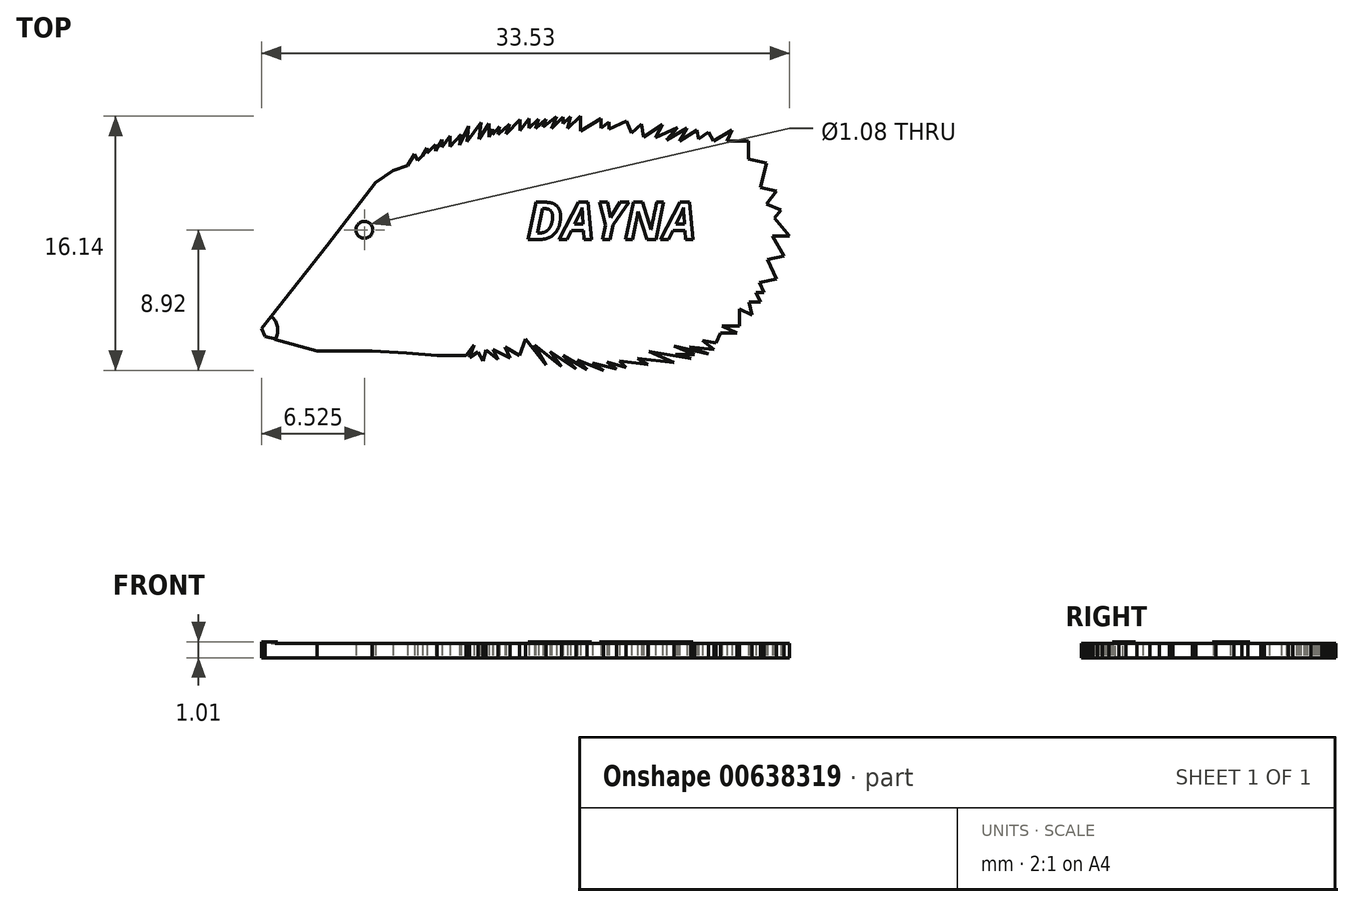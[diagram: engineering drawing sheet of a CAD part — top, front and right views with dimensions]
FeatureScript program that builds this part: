
annotation { "Feature Type Name" : "Feature", "Feature Type Description" : "" }
export const myFeature = defineFeature(function(context is Context, id is Id, definition is map)
    precondition{}
    {
        {
            var Q0;
            Q0=qCreatedBy(makeId("Top.planeOp"),FACE);
            var sketch = newSketch(context, id + "F0", { "sketchPlane" : qUnion([Q0])});
            skLineSegment(sketch, "E0", {"start": v(-31.15, -0.16) * mm, "end": v(-27, 5.13) * mm});
            skLineSegment(sketch, "E1", {"start": v(-27, 5.13) * mm, "end": v(-23.92, 9.12) * mm});
            skLineSegment(sketch, "E2", {"start": v(-23.92, 9.12) * mm, "end": v(-22.8, 9.88) * mm});
            skLineSegment(sketch, "E3", {"start": v(-22.8, 9.88) * mm, "end": v(-21.87, 10.2) * mm});
            skLineSegment(sketch, "E4", {"start": v(-21.87, 10.2) * mm, "end": v(-21.44, 10.95) * mm});
            skLineSegment(sketch, "E5", {"start": v(-21.44, 10.95) * mm, "end": v(-21.25, 10.51) * mm});
            skLineSegment(sketch, "E6", {"start": v(-21.25, 10.51) * mm, "end": v(-20.93, 10.85) * mm});
            skLineSegment(sketch, "E7", {"start": v(-20.93, 10.85) * mm, "end": v(-20.65, 11.31) * mm});
            skLineSegment(sketch, "E8", {"start": v(-20.65, 11.31) * mm, "end": v(-20.65, 11) * mm});
            skLineSegment(sketch, "E9", {"start": v(-20.65, 11) * mm, "end": v(-20.1, 11.54) * mm});
            skLineSegment(sketch, "E10", {"start": v(-20.1, 11.54) * mm, "end": v(-20.1, 11.12) * mm});
            skLineSegment(sketch, "E11", {"start": v(-20.1, 11.12) * mm, "end": v(-19.68, 11.84) * mm});
            skLineSegment(sketch, "E12", {"start": v(-19.68, 11.84) * mm, "end": v(-19.68, 11.37) * mm});
            skLineSegment(sketch, "E13", {"start": v(-19.68, 11.37) * mm, "end": v(-19.18, 12.06) * mm});
            skLineSegment(sketch, "E14", {"start": v(-19.18, 12.06) * mm, "end": v(-19.18, 11.42) * mm});
            skLineSegment(sketch, "E15", {"start": v(-19.18, 11.42) * mm, "end": v(-18.48, 12.16) * mm});
            skLineSegment(sketch, "E16", {"start": v(-18.48, 12.16) * mm, "end": v(-18.6, 11.5) * mm});
            skLineSegment(sketch, "E17", {"start": v(-18.6, 11.5) * mm, "end": v(-18, 12.7) * mm});
            skLineSegment(sketch, "E18", {"start": v(-18, 12.7) * mm, "end": v(-18.12, 11.72) * mm});
            skLineSegment(sketch, "E19", {"start": v(-18.12, 11.72) * mm, "end": v(-17.2, 12.94) * mm});
            skLineSegment(sketch, "E20", {"start": v(-17.2, 12.94) * mm, "end": v(-17.33, 11.88) * mm});
            skLineSegment(sketch, "E21", {"start": v(-17.33, 11.88) * mm, "end": v(-16.71, 12.88) * mm});
            skLineSegment(sketch, "E22", {"start": v(-16.71, 12.88) * mm, "end": v(-16.71, 12.01) * mm});
            skLineSegment(sketch, "E23", {"start": v(-16.71, 12.01) * mm, "end": v(-16.47, 12.52) * mm});
            skLineSegment(sketch, "E24", {"start": v(-16.47, 12.52) * mm, "end": v(-16.47, 12.16) * mm});
            skLineSegment(sketch, "E25", {"start": v(-16.47, 12.16) * mm, "end": v(-16.02, 12.68) * mm});
            skLineSegment(sketch, "E26", {"start": v(-16.02, 12.68) * mm, "end": v(-16.13, 12.18) * mm});
            skLineSegment(sketch, "E27", {"start": v(-16.13, 12.18) * mm, "end": v(-15.4, 12.85) * mm});
            skLineSegment(sketch, "E28", {"start": v(-15.4, 12.85) * mm, "end": v(-15.63, 12.2) * mm});
            skLineSegment(sketch, "E29", {"start": v(-15.63, 12.2) * mm, "end": v(-14.74, 13.13) * mm});
            skLineSegment(sketch, "E30", {"start": v(-14.74, 13.13) * mm, "end": v(-14.74, 12.44) * mm});
            skLineSegment(sketch, "E31", {"start": v(-14.74, 12.44) * mm, "end": v(-14.17, 13.18) * mm});
            skLineSegment(sketch, "E32", {"start": v(-14.17, 13.18) * mm, "end": v(-14.17, 12.58) * mm});
            skLineSegment(sketch, "E33", {"start": v(-14.17, 12.58) * mm, "end": v(-13.58, 13.14) * mm});
            skLineSegment(sketch, "E34", {"start": v(-13.58, 13.14) * mm, "end": v(-13.74, 12.56) * mm});
            skLineSegment(sketch, "E35", {"start": v(-13.74, 12.56) * mm, "end": v(-13.09, 13.16) * mm});
            skLineSegment(sketch, "E36", {"start": v(-13.09, 13.16) * mm, "end": v(-13.29, 12.65) * mm});
            skLineSegment(sketch, "E37", {"start": v(-13.29, 12.65) * mm, "end": v(-12.43, 13.32) * mm});
            skLineSegment(sketch, "E38", {"start": v(-12.43, 13.32) * mm, "end": v(-12.74, 12.56) * mm});
            skLineSegment(sketch, "E39", {"start": v(-12.74, 12.56) * mm, "end": v(-12.02, 13.27) * mm});
            skLineSegment(sketch, "E40", {"start": v(-12.02, 13.27) * mm, "end": v(-12.02, 12.87) * mm});
            skLineSegment(sketch, "E41", {"start": v(-12.02, 12.87) * mm, "end": v(-11.54, 13.3) * mm});
            skLineSegment(sketch, "E42", {"start": v(-11.54, 13.3) * mm, "end": v(-11.7, 12.56) * mm});
            skLineSegment(sketch, "E43", {"start": v(-11.7, 12.56) * mm, "end": v(-10.9, 13.34) * mm});
            skLineSegment(sketch, "E44", {"start": v(-10.9, 13.34) * mm, "end": v(-10.9, 12.4) * mm});
            skLineSegment(sketch, "E45", {"start": v(-10.9, 12.4) * mm, "end": v(-9.59, 13.2) * mm});
            skLineSegment(sketch, "E46", {"start": v(-9.59, 13.2) * mm, "end": v(-9.59, 12.6) * mm});
            skLineSegment(sketch, "E47", {"start": v(-9.59, 12.6) * mm, "end": v(-9.08, 12.98) * mm});
            skLineSegment(sketch, "E48", {"start": v(-9.08, 12.98) * mm, "end": v(-9.08, 12.53) * mm});
            skLineSegment(sketch, "E49", {"start": v(-9.08, 12.53) * mm, "end": v(-7.99, 13.02) * mm});
            skLineSegment(sketch, "E50", {"start": v(-7.99, 13.02) * mm, "end": v(-7.65, 12.26) * mm});
            skLineSegment(sketch, "E51", {"start": v(-7.65, 12.26) * mm, "end": v(-7.03, 12.83) * mm});
            skLineSegment(sketch, "E52", {"start": v(-7.03, 12.83) * mm, "end": v(-6.9, 12.02) * mm});
            skLineSegment(sketch, "E53", {"start": v(-6.9, 12.02) * mm, "end": v(-5.7, 12.82) * mm});
            skLineSegment(sketch, "E54", {"start": v(-5.7, 12.82) * mm, "end": v(-6.12, 11.98) * mm});
            skLineSegment(sketch, "E55", {"start": v(-6.12, 11.98) * mm, "end": v(-4.74, 12.62) * mm});
            skLineSegment(sketch, "E56", {"start": v(-4.74, 12.62) * mm, "end": v(-5.43, 11.84) * mm});
            skLineSegment(sketch, "E57", {"start": v(-5.43, 11.84) * mm, "end": v(-4.14, 12.58) * mm});
            skLineSegment(sketch, "E58", {"start": v(-4.14, 12.58) * mm, "end": v(-4.6, 11.76) * mm});
            skLineSegment(sketch, "E59", {"start": v(-4.6, 11.76) * mm, "end": v(-3.5, 12.45) * mm});
            skLineSegment(sketch, "E60", {"start": v(-3.5, 12.45) * mm, "end": v(-3.39, 11.87) * mm});
            skLineSegment(sketch, "E61", {"start": v(-3.39, 11.87) * mm, "end": v(-2.76, 12.33) * mm});
            skLineSegment(sketch, "E62", {"start": v(-2.76, 12.33) * mm, "end": v(-2.44, 11.76) * mm});
            skLineSegment(sketch, "E63", {"start": v(-2.44, 11.76) * mm, "end": v(-1.26, 12.45) * mm});
            skLineSegment(sketch, "E64", {"start": v(-1.26, 12.45) * mm, "end": v(-1.59, 11.76) * mm});
            skLineSegment(sketch, "E65", {"start": v(-1.59, 11.76) * mm, "end": v(-0.23, 11.76) * mm});
            skLineSegment(sketch, "E66", {"start": v(-0.23, 11.76) * mm, "end": v(-0.23, 10.62) * mm});
            skLineSegment(sketch, "E67", {"start": v(-0.23, 10.62) * mm, "end": v(0.91, 10.35) * mm});
            skLineSegment(sketch, "E68", {"start": v(0.91, 10.35) * mm, "end": v(0.55, 8.82) * mm});
            skLineSegment(sketch, "E69", {"start": v(0.55, 8.82) * mm, "end": v(1.56, 8.58) * mm});
            skLineSegment(sketch, "E70", {"start": v(1.56, 8.58) * mm, "end": v(0.91, 7.76) * mm});
            skLineSegment(sketch, "E71", {"start": v(0.91, 7.76) * mm, "end": v(1.84, 7.38) * mm});
            skLineSegment(sketch, "E72", {"start": v(1.84, 7.38) * mm, "end": v(1.42, 6.86) * mm});
            skLineSegment(sketch, "E73", {"start": v(1.42, 6.86) * mm, "end": v(2.38, 5.73) * mm});
            skLineSegment(sketch, "E74", {"start": v(2.38, 5.73) * mm, "end": v(1.3, 5.73) * mm});
            skLineSegment(sketch, "E75", {"start": v(1.3, 5.73) * mm, "end": v(2.02, 4.47) * mm});
            skLineSegment(sketch, "E76", {"start": v(2.02, 4.47) * mm, "end": v(0.97, 4.23) * mm});
            skLineSegment(sketch, "E77", {"start": v(0.97, 4.23) * mm, "end": v(1.54, 3) * mm});
            skLineSegment(sketch, "E78", {"start": v(1.54, 3) * mm, "end": v(0.48, 2.76) * mm});
            skLineSegment(sketch, "E79", {"start": v(0.48, 2.76) * mm, "end": v(0.76, 2.15) * mm});
            skLineSegment(sketch, "E80", {"start": v(0.76, 2.15) * mm, "end": v(0.26, 2.15) * mm});
            skLineSegment(sketch, "E81", {"start": v(0.26, 2.15) * mm, "end": v(0.55, 1.54) * mm});
            skLineSegment(sketch, "E82", {"start": v(0.55, 1.54) * mm, "end": v(-0.21, 1.54) * mm});
            skLineSegment(sketch, "E83", {"start": v(-0.21, 1.54) * mm, "end": v(0, 0.72) * mm});
            skLineSegment(sketch, "E84", {"start": v(0, 0.72) * mm, "end": v(-0.8, 1.08) * mm});
            skLineSegment(sketch, "E85", {"start": v(-0.8, 1.08) * mm, "end": v(-0.8, 0) * mm});
            skLineSegment(sketch, "E86", {"start": v(-0.8, 0) * mm, "end": v(-1.91, 0) * mm});
            skLineSegment(sketch, "E87", {"start": v(-1.91, 0) * mm, "end": v(-0.97, -0.44) * mm});
            skLineSegment(sketch, "E88", {"start": v(-0.97, -0.44) * mm, "end": v(-2.02, -0.44) * mm});
            skLineSegment(sketch, "E89", {"start": v(-2.02, -0.44) * mm, "end": v(-2.3, -1.06) * mm});
            skLineSegment(sketch, "E90", {"start": v(-2.3, -1.06) * mm, "end": v(-3.16, -0.91) * mm});
            skLineSegment(sketch, "E91", {"start": v(-3.16, -0.91) * mm, "end": v(-2.43, -1.48) * mm});
            skLineSegment(sketch, "E92", {"start": v(-2.43, -1.48) * mm, "end": v(-3.99, -1.33) * mm});
            skLineSegment(sketch, "E93", {"start": v(-3.99, -1.33) * mm, "end": v(-2.75, -1.78) * mm});
            skLineSegment(sketch, "E94", {"start": v(-2.75, -1.78) * mm, "end": v(-4.95, -1.25) * mm});
            skLineSegment(sketch, "E95", {"start": v(-4.95, -1.25) * mm, "end": v(-3.66, -1.81) * mm});
            skLineSegment(sketch, "E96", {"start": v(-3.66, -1.81) * mm, "end": v(-4.87, -1.81) * mm});
            skLineSegment(sketch, "E97", {"start": v(-4.87, -1.81) * mm, "end": v(-3.9, -2.07) * mm});
            skLineSegment(sketch, "E98", {"start": v(-3.9, -2.07) * mm, "end": v(-6.56, -1.62) * mm});
            skLineSegment(sketch, "E99", {"start": v(-6.56, -1.62) * mm, "end": v(-4.95, -2.3) * mm});
            skLineSegment(sketch, "E100", {"start": v(-4.95, -2.3) * mm, "end": v(-7.3, -2.05) * mm});
            skLineSegment(sketch, "E101", {"start": v(-7.3, -2.05) * mm, "end": v(-6.6, -2.45) * mm});
            skLineSegment(sketch, "E102", {"start": v(-6.6, -2.45) * mm, "end": v(-8.4, -2.2) * mm});
            skLineSegment(sketch, "E103", {"start": v(-8.4, -2.2) * mm, "end": v(-8, -2.63) * mm});
            skLineSegment(sketch, "E104", {"start": v(-8, -2.63) * mm, "end": v(-9.22, -2.26) * mm});
            skLineSegment(sketch, "E105", {"start": v(-9.22, -2.26) * mm, "end": v(-8.62, -2.73) * mm});
            skLineSegment(sketch, "E106", {"start": v(-8.62, -2.73) * mm, "end": v(-10.14, -2.34) * mm});
            skLineSegment(sketch, "E107", {"start": v(-10.14, -2.34) * mm, "end": v(-9.43, -2.8) * mm});
            skLineSegment(sketch, "E108", {"start": v(-9.43, -2.8) * mm, "end": v(-11.09, -2.14) * mm});
            skLineSegment(sketch, "E109", {"start": v(-11.09, -2.14) * mm, "end": v(-10.5, -2.74) * mm});
            skLineSegment(sketch, "E110", {"start": v(-10.5, -2.74) * mm, "end": v(-12.02, -1.87) * mm});
            skLineSegment(sketch, "E111", {"start": v(-12.02, -1.87) * mm, "end": v(-11.17, -2.72) * mm});
            skLineSegment(sketch, "E112", {"start": v(-11.17, -2.72) * mm, "end": v(-12.82, -1.62) * mm});
            skLineSegment(sketch, "E113", {"start": v(-12.82, -1.62) * mm, "end": v(-12.1, -2.55) * mm});
            skLineSegment(sketch, "E114", {"start": v(-12.1, -2.55) * mm, "end": v(-13.81, -1.2) * mm});
            skLineSegment(sketch, "E115", {"start": v(-13.81, -1.2) * mm, "end": v(-13.09, -2.45) * mm});
            skLineSegment(sketch, "E116", {"start": v(-13.09, -2.45) * mm, "end": v(-14.4, -0.81) * mm});
            skLineSegment(sketch, "E117", {"start": v(-14.4, -0.81) * mm, "end": v(-14.78, -1.87) * mm});
            skLineSegment(sketch, "E118", {"start": v(-14.78, -1.87) * mm, "end": v(-15.69, -1.32) * mm});
            skLineSegment(sketch, "E119", {"start": v(-15.69, -1.32) * mm, "end": v(-15.37, -2.02) * mm});
            skLineSegment(sketch, "E120", {"start": v(-15.37, -2.02) * mm, "end": v(-16.44, -1.48) * mm});
            skLineSegment(sketch, "E121", {"start": v(-16.44, -1.48) * mm, "end": v(-16.15, -2.11) * mm});
            skLineSegment(sketch, "E122", {"start": v(-16.15, -2.11) * mm, "end": v(-16.91, -1.52) * mm});
            skLineSegment(sketch, "E123", {"start": v(-16.91, -1.52) * mm, "end": v(-17.07, -2.2) * mm});
            skLineSegment(sketch, "E124", {"start": v(-17.07, -2.2) * mm, "end": v(-17.4, -1.65) * mm});
            skLineSegment(sketch, "E125", {"start": v(-17.4, -1.65) * mm, "end": v(-17.95, -1.97) * mm});
            skLineSegment(sketch, "E126", {"start": v(-17.95, -1.97) * mm, "end": v(-17.66, -1.2) * mm});
            skLineSegment(sketch, "E127", {"start": v(-17.66, -1.2) * mm, "end": v(-18.18, -1.87) * mm});
            skLineSegment(sketch, "E128", {"start": v(-18.18, -1.87) * mm, "end": v(-20.02, -1.87) * mm});
            skLineSegment(sketch, "E129", {"start": v(-20.02, -1.87) * mm, "end": v(-21.95, -1.72) * mm});
            skLineSegment(sketch, "E130", {"start": v(-21.95, -1.72) * mm, "end": v(-24.13, -1.56) * mm});
            skLineSegment(sketch, "E131", {"start": v(-24.13, -1.56) * mm, "end": v(-27.64, -1.56) * mm});
            skLineSegment(sketch, "E132", {"start": v(-27.64, -1.56) * mm, "end": v(-30.94, -0.66) * mm});
            skLineSegment(sketch, "E133", {"start": v(-30.94, -0.66) * mm, "end": v(-31.15, -0.16) * mm});
            skCircle(sketch, "E134", {"center": v(-24.62, 6.12) * mm, "radius": 0.54 * mm});
            skSolve(sketch);
        }
        {
            var Q0;
            Q0 = qSketchRegion(id + "F0", true);
            extrude(context, id + "F1", {"entities" : qUnion([Q0]), "depth" : 0.9 * mm, "offsetDistance" : 25.4 * mm});
        }
        {
            var Q0;
            Q0=qCreatedBy(makeId("Top.planeOp"),FACE);
            var sketch = newSketch(context, id + "F2", { "sketchPlane" : qUnion([Q0])});
            skText(sketch, "E135", { "text": "DAYNA", "fontName": "OpenSans-BoldItalic.ttf"});
            const initialGuessF2  = {"E135": [-0.0143, 0.00551, 1, 0, 0.00238]};
            skSetInitialGuess(sketch, initialGuessF2);
            skSolve(sketch);
        }
        {
            var Q0;
            Q0 = qSketchRegion(id + "F2", true);
            extrude(context, id + "F3", {"entities" : qUnion([Q0]), "operationType" : NewBodyOperationType.ADD, "depth" : 1 * mm, "offsetDistance" : 25 * mm});
        }
        {
            var Q0;
            Q0=qCreatedBy(makeId("Top.planeOp"),FACE);
            var sketch = newSketch(context, id + "F4", { "sketchPlane" : qUnion([Q0])});
            skArc(sketch, "E136", {"start": v(-30.28, -0.83) * mm, "mid": v(-30.14, -0.05) * mm, "end": v(-30.54, 0.63) * mm});
            skLineSegment(sketch, "E137", {"start": v(-30.54, 0.63) * mm, "end": v(-31.15, -0.15) * mm});
            skLineSegment(sketch, "E138", {"start": v(-31.15, -0.15) * mm, "end": v(-30.94, -0.66) * mm});
            skLineSegment(sketch, "E139", {"start": v(-30.94, -0.66) * mm, "end": v(-30.28, -0.83) * mm});
            skSolve(sketch);
        }
        {
            var Q0;
            Q0 = qSketchRegion(id + "F4", true);
            extrude(context, id + "F5", {"entities" : qUnion([Q0]), "operationType" : NewBodyOperationType.ADD, "depth" : 1.01 * mm, "offsetDistance" : 25 * mm});
        }
    });
